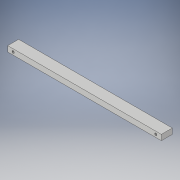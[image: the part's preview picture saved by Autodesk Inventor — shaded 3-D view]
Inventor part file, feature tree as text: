
AUTODESK INVENTOR PART (.ipt)
format: ipt  version: 2017 (Build 210142000, 142)  size: 105,984 bytes
history: native  units: in
note: dims shown in document units (in); Inventor stores cm internally (conversion verified against a paired STEP export)
features: sketch x2, extrude x1, hole x1
ambient origin geometry x8: Origin, YZ Plane, XZ Plane, XY Plane, X Axis, Y Axis, Z Axis, Center Point
bodies: Solid1 (feature_tree)
feature tree (4):
  extrude  "Extrusion1"  Depth=0.25in
  hole  "Hole1"  [1 undecoded]
  sketch  "Sketch1"  dims[d0=7.016in d1=0.25in]
  sketch  "Sketch2"  dims[d2=0.5in d3=0.0in d4=0.25in d5=0.25in d6=0.14in d7=0.14in d10=0.104in d11=0.5in d12=0.375in d13=0.25in d14=0.5635in d15=0.5in d16=0.8108in]
note: 1 required parameter value undecoded (feature->parameter linkage not recoverable at this tier; creation-order binding heuristic only, values carry confidence <= 0.55)
